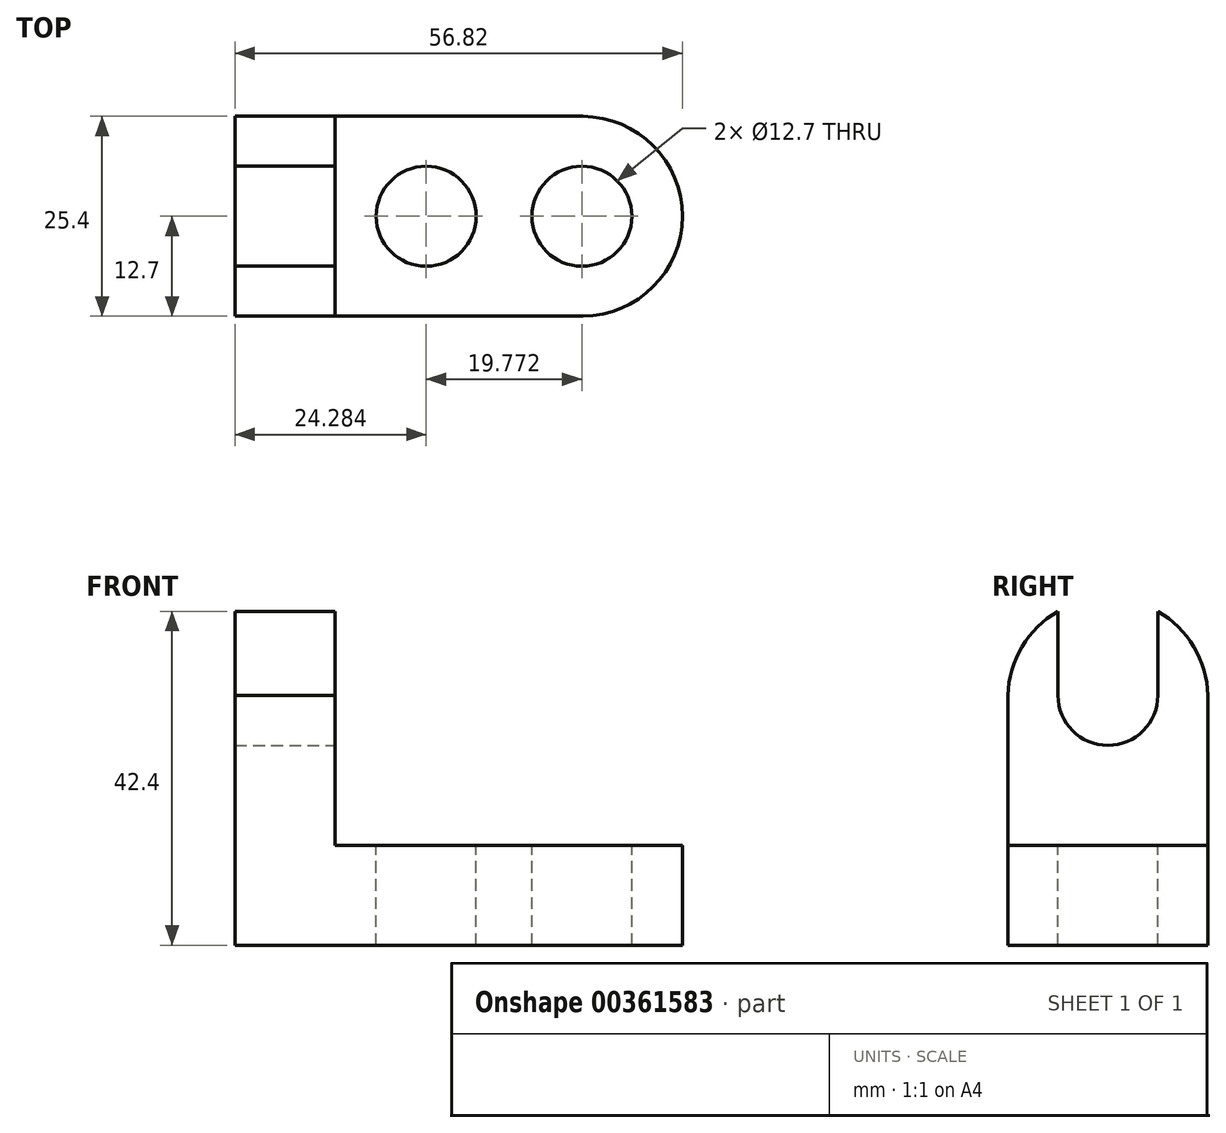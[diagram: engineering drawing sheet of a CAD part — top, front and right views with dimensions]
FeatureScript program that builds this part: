
annotation { "Feature Type Name" : "Feature", "Feature Type Description" : "" }
export const myFeature = defineFeature(function(context is Context, id is Id, definition is map)
    precondition{}
    {
        {
            var Q0;
            Q0=qCreatedBy(makeId("Front.planeOp"),FACE);
            var sketch = newSketch(context, id + "F0", { "sketchPlane" : qUnion([Q0])});
            skLineSegment(sketch, "E0", {"start": v(0, 0) * mm, "end": v(57.15, 0) * mm});
            skLineSegment(sketch, "E1", {"start": v(57.15, 0) * mm, "end": v(57.15, 12.7) * mm});
            skLineSegment(sketch, "E2", {"start": v(57.15, 12.7) * mm, "end": v(12.7, 12.7) * mm});
            skLineSegment(sketch, "E3", {"start": v(12.7, 12.7) * mm, "end": v(12.7, 44.45) * mm});
            skLineSegment(sketch, "E4", {"start": v(12.7, 44.45) * mm, "end": v(0, 44.45) * mm});
            skLineSegment(sketch, "E5", {"start": v(0, 44.45) * mm, "end": v(0, 0) * mm});
            skSolve(sketch);
        }
        {
            var Q0;
            Q0=makeQuery(id+"F0.imprint","IMPRINT",FACE,{"disambiguationData":[TD([[makeQuery(id+"F0.imprint","IMPRINT",EDGE,{"derivedFrom":sQuery(id+"F0.wireOp",EDGE,"E0")}),1.0]])]});
            extrude(context, id + "F1", {"entities" : qUnion([Q0]), "depth" : 25.4 * mm});
        }
        {
            var Q0;
            Q0=makeQuery(id+"F1.opExtrude","SWEPT_FACE",FACE,{"disambiguationData":[OSD([sQuery(id+"F0.wireOp",EDGE,"E3")])]});
            var sketch = newSketch(context, id + "F2", { "sketchPlane" : qUnion([Q0])});
            skCircle(sketch, "E6", {"center": v(-12.7, 31.75) * mm, "radius": 6.35 * mm});
            skLineSegment(sketch, "E7", {"start": v(-19.05, 31.75) * mm, "end": v(-19.05, 44.45) * mm});
            skLineSegment(sketch, "E8", {"start": v(-6.35, 31.75) * mm, "end": v(-6.35, 44.45) * mm});
            skArc(sketch, "E9", {"start": v(0, 31.75) * mm, "mid": v(-12.7, 44.1) * mm, "end": v(-25.4, 31.75) * mm});
            skSolve(sketch);
        }
        {
            var Q0;
            {var subQ1=sQuery(id+"F0.wireOp",EDGE,"E3");var subQ4=sQuery(id+"F2.wireOp",EDGE,"E9");var subQ6=makeQuery(id+"F1.opExtrude","CAP_EDGE",EDGE,{"disambiguationData":[OSD([subQ1])],"isStart":false});var subQ7=makeQuery(id+"F2.imprint","INTERSECT",VERTEX,{"derivedFrom":[subQ6,subQ4]});Q0=makeQuery(id+"F2.imprint","IMPRINT",FACE,{"disambiguationData":[TD([[makeQuery(id+"F2.imprint","IMPRINT",EDGE,{"disambiguationData":[TD([[subQ7,1.0]])],"derivedFrom":subQ4}),-1.0]])]});}
            var Q1;
            {var subQ0=sQuery(id+"F2.wireOp",EDGE,"E7");var subQ3=sQuery(id+"F2.wireOp",EDGE,"E9");var subQ4=makeQuery(id+"F2.imprint","INTERSECT",VERTEX,{"derivedFrom":[subQ0,subQ3]});Q1=makeQuery(id+"F2.imprint","IMPRINT",FACE,{"disambiguationData":[TD([[makeQuery(id+"F2.imprint","IMPRINT",EDGE,{"disambiguationData":[TD([[subQ4,1.0]])],"derivedFrom":subQ3}),-1.0]])]});}
            var Q2;
            {var subQ0=sQuery(id+"F2.wireOp",EDGE,"E7");var subQ1=sQuery(id+"F2.wireOp",EDGE,"E6");var subQ2=makeQuery(id+"F2.imprint","INTERSECT",VERTEX,{"derivedFrom":[subQ1,subQ0]});Q2=makeQuery(id+"F2.imprint","IMPRINT",FACE,{"disambiguationData":[TD([[makeQuery(id+"F2.imprint","IMPRINT",EDGE,{"disambiguationData":[TD([[subQ2,1.0]])],"derivedFrom":subQ1}),-1.0]])]});}
            var Q3;
            {var subQ0=sQuery(id+"F2.wireOp",EDGE,"E6");var subQ1=makeQuery(id+"F2.imprint","INTERSECT",VERTEX,{"derivedFrom":[subQ0,sQuery(id+"F2.wireOp",EDGE,"E7")]});Q3=makeQuery(id+"F2.imprint","IMPRINT",FACE,{"disambiguationData":[TD([[makeQuery(id+"F2.imprint","IMPRINT",EDGE,{"disambiguationData":[TD([[subQ1,1.0]])],"derivedFrom":subQ0}),1.0]])]});}
            var Q4;
            {var subQ1=sQuery(id+"F0.wireOp",EDGE,"E3");var subQ4=sQuery(id+"F2.wireOp",EDGE,"E9");var subQ6=makeQuery(id+"F1.opExtrude","CAP_EDGE",EDGE,{"disambiguationData":[OSD([subQ1])],"isStart":true});var subQ8=makeQuery(id+"F2.imprint","INTERSECT",VERTEX,{"derivedFrom":[subQ6,subQ4]});Q4=makeQuery(id+"F2.imprint","IMPRINT",FACE,{"disambiguationData":[TD([[makeQuery(id+"F2.imprint","IMPRINT",EDGE,{"disambiguationData":[TD([[subQ8,-1.0]])],"derivedFrom":subQ4}),-1.0]])]});}
            extrude(context, id + "F3", {"entities" : qUnion([Q0, Q1, Q2, Q3, Q4]), "operationType" : NewBodyOperationType.REMOVE, "oppositeDirection" : true, "depth" : 12.7 * mm});
        }
        {
            var Q0;
            Q0=makeQuery(id+"F1.opExtrude","SWEPT_FACE",FACE,{"disambiguationData":[OSD([sQuery(id+"F0.wireOp",EDGE,"E2")])]});
            var sketch = newSketch(context, id + "F4", { "sketchPlane" : qUnion([Q0])});
            skCircle(sketch, "E10", {"center": v(24.28, -12.7) * mm, "radius": 6.35 * mm});
            skCircle(sketch, "E11", {"center": v(44.06, -12.7) * mm, "radius": 6.35 * mm});
            skArc(sketch, "E12", {"start": v(44.06, -25.4) * mm, "mid": v(56.82, -12.7) * mm, "end": v(44.06, 0) * mm});
            skSolve(sketch);
        }
        {
            var Q0;
            Q0=makeQuery(id+"F4.imprint","IMPRINT",FACE,{"disambiguationData":[TD([[makeQuery(id+"F4.imprint","IMPRINT",EDGE,{"derivedFrom":sQuery(id+"F4.wireOp",EDGE,"E10")}),1.0]])]});
            var Q1;
            Q1=makeQuery(id+"F4.imprint","IMPRINT",FACE,{"disambiguationData":[TD([[makeQuery(id+"F4.imprint","IMPRINT",EDGE,{"derivedFrom":sQuery(id+"F4.wireOp",EDGE,"E11")}),1.0]])]});
            var Q2;
            {var subQ1=sQuery(id+"F0.wireOp",EDGE,"E2");var subQ6=makeQuery(id+"F1.opExtrude","SWEPT_EDGE",EDGE,{"disambiguationData":[OSD([sQuery(id+"F0.wireOp",EDGE,"E1"),subQ1])]});Q2=makeQuery(id+"F4.imprint","IMPRINT",FACE,{"disambiguationData":[TD([[makeQuery(id+"F4.imprint","IMPRINT",EDGE,{"derivedFrom":subQ6}),1.0]])]});}
            extrude(context, id + "F5", {"entities" : qUnion([Q0, Q1, Q2]), "operationType" : NewBodyOperationType.REMOVE, "oppositeDirection" : true, "depth" : 12.7 * mm});
        }
    });
